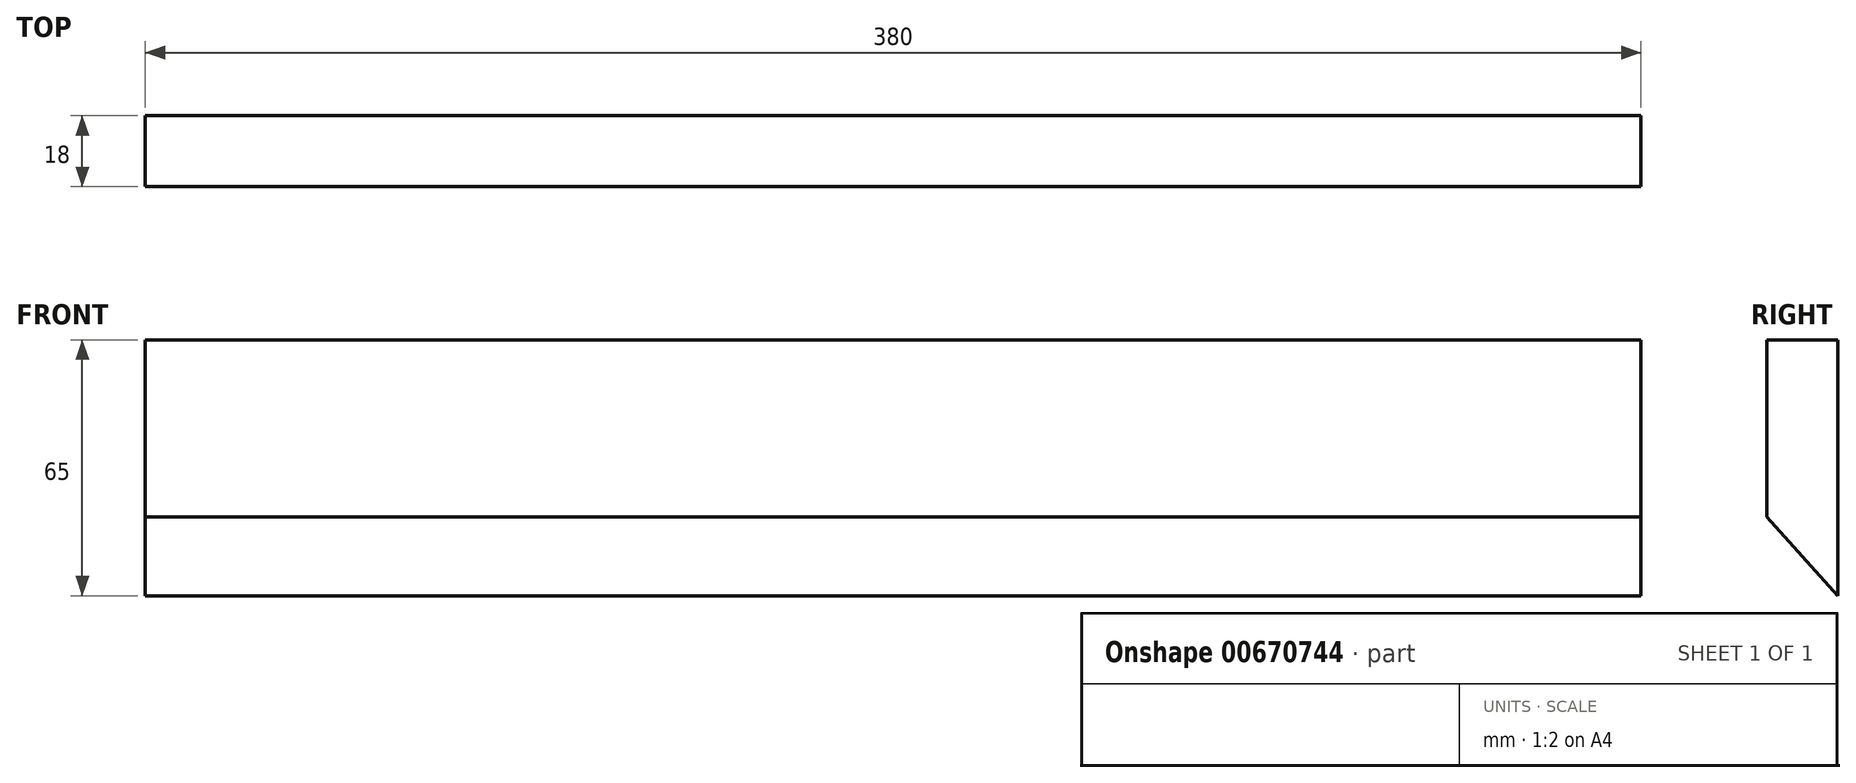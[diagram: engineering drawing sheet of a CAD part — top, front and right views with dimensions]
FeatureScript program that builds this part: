
annotation { "Feature Type Name" : "Feature", "Feature Type Description" : "" }
export const myFeature = defineFeature(function(context is Context, id is Id, definition is map)
    precondition{}
    {
        {
            var Q0;
            Q0=qCreatedBy(makeId("Right.planeOp"),FACE);
            var sketch = newSketch(context, id + "F0", { "sketchPlane" : qUnion([Q0])});
            skLineSegment(sketch, "E0", {"start": v(-9, 32.5) * mm, "end": v(9, 32.5) * mm});
            skLineSegment(sketch, "E1", {"start": v(9, 32.5) * mm, "end": v(9, -32.5) * mm});
            skLineSegment(sketch, "E2", {"start": v(9, -32.5) * mm, "end": v(-9, -12.5) * mm});
            skLineSegment(sketch, "E3", {"start": v(-9, -12.5) * mm, "end": v(-9, 32.5) * mm});
            skSolve(sketch);
        }
        {
            var Q0;
            Q0 = qSketchRegion(id + "F0", true);
            extrude(context, id + "F1", {"entities" : qUnion([Q0]), "endBound" : BoundingType.SYMMETRIC, "depth" : 380 * mm, "offsetDistance" : 25 * mm});
        }
    });
